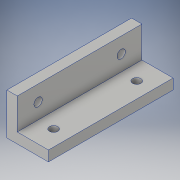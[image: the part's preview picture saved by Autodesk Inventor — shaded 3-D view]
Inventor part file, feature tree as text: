
AUTODESK INVENTOR PART (.ipt)
format: ipt  version: 2018 (Build 220112000, 112)  size: 126,976 bytes
history: native  units: in
note: dims shown in document units (in); Inventor stores cm internally (conversion verified against a paired STEP export)
features: extrude x3, sketch x3
ambient origin geometry x8: Origin, YZ Plane, XZ Plane, XY Plane, X Axis, Y Axis, Z Axis, Center Point
bodies: Solid1 (feature_tree)
feature tree (6):
  extrude  "Extrusion1"  Depth=0.25in
  extrude  "Extrusion2"  Depth=1.0in
  extrude  "Extrusion3"  Depth=0.75in
  sketch  "Sketch1"  dims[d0=1.0in d1=0.25in]
  sketch  "Sketch2"  dims[d2=0.25in d3=1.0in]
  sketch  "Sketch3"  dims[d4=3.0in d5=0.0in d6=0.75in d7=0.5in d8=0.5in d9=0.2in d10=0.2in d11=1.0in d12=0.0in d13=0.5in d14=0.5in d15=0.2in d16=1.0in d17=0.0in]
